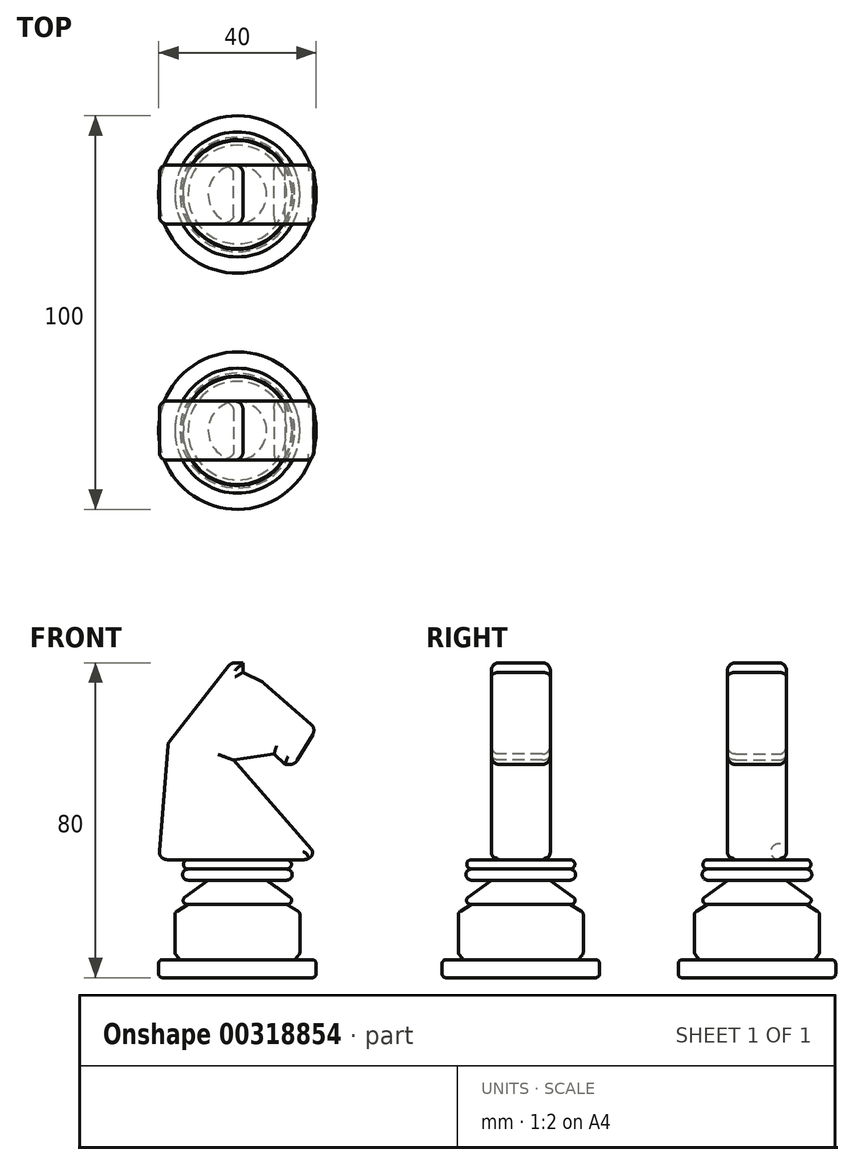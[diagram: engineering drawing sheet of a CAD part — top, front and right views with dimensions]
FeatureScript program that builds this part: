
annotation { "Feature Type Name" : "Feature", "Feature Type Description" : "" }
export const myFeature = defineFeature(function(context is Context, id is Id, definition is map)
    precondition{}
    {
        {
            var Q0;
            Q0=qCreatedBy(makeId("Front.planeOp"),FACE);
            var sketch = newSketch(context, id + "F0", { "sketchPlane" : qUnion([Q0])});
            skLineSegment(sketch, "E0", {"start": v(-20, -50) * mm, "end": v(0, -50) * mm});
            skLineSegment(sketch, "E1", {"start": v(0, -20) * mm, "end": v(-41.16, -20) * mm, "construction": true});
            skLineSegment(sketch, "E2", {"start": v(-20, -50) * mm, "end": v(-20, -45.41) * mm});
            skLineSegment(sketch, "E3", {"start": v(-20, -45.41) * mm, "end": v(-14.57, -45.41) * mm});
            skLineSegment(sketch, "E4", {"start": v(-14.57, -45.41) * mm, "end": v(-15.86, -43.88) * mm});
            skLineSegment(sketch, "E5", {"start": v(-15.86, -43.88) * mm, "end": v(-15.86, -33.4) * mm});
            skLineSegment(sketch, "E6", {"start": v(-15.86, -33.4) * mm, "end": v(-12.53, -31.35) * mm});
            skLineSegment(sketch, "E7", {"start": v(-12.53, -31.35) * mm, "end": v(-15.86, -31.35) * mm});
            skLineSegment(sketch, "E8", {"start": v(-15.86, -31.35) * mm, "end": v(-7.41, -25.21) * mm});
            skLineSegment(sketch, "E9", {"start": v(-7.41, -25.21) * mm, "end": v(-12.53, -25.21) * mm});
            skArc(sketch, "E10", {"start": v(-12.53, -22.4) * mm, "mid": v(-13.93, -23.8) * mm, "end": v(-12.53, -25.21) * mm});
            skLineSegment(sketch, "E11", {"start": v(-12.53, -22.4) * mm, "end": v(-10.23, -22.4) * mm});
            skArc(sketch, "E12", {"start": v(-12.53, -20) * mm, "mid": v(-13.73, -21.2) * mm, "end": v(-12.53, -22.4) * mm});
            skLineSegment(sketch, "E13", {"start": v(-12.53, -20) * mm, "end": v(0, -20) * mm});
            skLineSegment(sketch, "E14", {"start": v(0, -20) * mm, "end": v(0, -50) * mm});
            skLineSegment(sketch, "E15", {"start": v(0, 50.5) * mm, "end": v(0, -69.42) * mm, "construction": true});
            skSolve(sketch);
        }
        {
            var Q0;
            Q0=makeQuery(id+"F0.imprint","IMPRINT",FACE,{"disambiguationData":[TD([[makeQuery(id+"F0.imprint","IMPRINT",EDGE,{"derivedFrom":sQuery(id+"F0.wireOp",EDGE,"E0")}),1.0]])]});
            var Q1;
            Q1=sQuery(id+"F0.wireOp",EDGE,"E15");
            revolve(context, id + "F1", {"entities" : qUnion([Q0]), "axis" : qUnion([Q1]), "revolveType" : RevolveType.FULL});
        }
        {
            var Q0;
            Q0=makeQuery(id+"F1.opRevolve","SWEPT_EDGE",EDGE,{"disambiguationData":[OSD([sQuery(id+"F0.wireOp",EDGE,"E0"),sQuery(id+"F0.wireOp",EDGE,"E2")])]});
            var Q1;
            Q1=makeQuery(id+"F1.opRevolve","SWEPT_EDGE",EDGE,{"disambiguationData":[OSD([sQuery(id+"F0.wireOp",EDGE,"E2"),sQuery(id+"F0.wireOp",EDGE,"E3")])]});
            var Q2;
            Q2=makeQuery(id+"F1.opRevolve","SWEPT_EDGE",EDGE,{"disambiguationData":[OSD([sQuery(id+"F0.wireOp",EDGE,"E5"),sQuery(id+"F0.wireOp",EDGE,"E6")])]});
            var Q3;
            Q3=makeQuery(id+"F1.opRevolve","SWEPT_EDGE",EDGE,{"disambiguationData":[OSD([sQuery(id+"F0.wireOp",EDGE,"E7"),sQuery(id+"F0.wireOp",EDGE,"E8")])]});
            var Q4;
            Q4=makeQuery(id+"F1.opRevolve","SWEPT_EDGE",EDGE,{"disambiguationData":[OSD([sQuery(id+"F0.wireOp",EDGE,"E4"),sQuery(id+"F0.wireOp",EDGE,"E5")])]});
            fillet(context, id + "F2", {"entities" : qUnion([Q0, Q1, Q2, Q3, Q4]), "radius" : 1 * mm, "tangentPropagation" : true, "allowEdgeOverflow" : false});
        }
        {
            var Q0;
            Q0=qCreatedBy(makeId("Front.planeOp"),FACE);
            var sketch = newSketch(context, id + "F3", { "sketchPlane" : qUnion([Q0])});
            skLineSegment(sketch, "E16", {"start": v(-20, -10) * mm, "end": v(-17.6, 19.6) * mm});
            skLineSegment(sketch, "E17", {"start": v(-17.6, 19.6) * mm, "end": v(-1.6, 40) * mm});
            skLineSegment(sketch, "E18", {"start": v(6.6, 35) * mm, "end": v(20, 23.3) * mm});
            skPoint(sketch, "E19.end.orphan", {"position": v(0.26, -10) * mm});
            skLineSegment(sketch, "E20", {"start": v(-20, -10) * mm, "end": v(0.26, -10) * mm});
            skPoint(sketch, "E21.end.orphan", {"position": v(0, 40) * mm});
            skLineSegment(sketch, "E22", {"start": v(-1.6, 40) * mm, "end": v(1.4, 40) * mm});
            skPoint(sketch, "E23.start.orphan", {"position": v(0, 37.6) * mm});
            skLineSegment(sketch, "E24", {"start": v(1.4, 40) * mm, "end": v(1.4, 37.6) * mm});
            skLineSegment(sketch, "E25", {"start": v(1.4, 37.6) * mm, "end": v(6.6, 35) * mm});
            skPoint(sketch, "E26.start.orphan", {"position": v(12.05, 14.2) * mm});
            skLineSegment(sketch, "E27", {"start": v(20, 23.3) * mm, "end": v(14.6, 14.2) * mm});
            skLineSegment(sketch, "E28", {"start": v(14.6, 14.2) * mm, "end": v(11.8, 14.2) * mm});
            skPoint(sketch, "E29.start.orphan", {"position": v(6.6, 16.7) * mm});
            skLineSegment(sketch, "E30", {"start": v(12.05, 14.2) * mm, "end": v(9.3, 16.8) * mm});
            skPoint(sketch, "E31.start.orphan", {"position": v(5.4, 14.2) * mm});
            skLineSegment(sketch, "E32", {"start": v(9.3, 16.8) * mm, "end": v(-1, 15.3) * mm});
            skLineSegment(sketch, "E33", {"start": v(-1, 15.3) * mm, "end": v(20, -8.7) * mm});
            skPoint(sketch, "E34.orphan", {"position": v(19.9, -10) * mm});
            skLineSegment(sketch, "E35", {"start": v(20, -8.7) * mm, "end": v(17.4, -10) * mm});
            skLineSegment(sketch, "E36", {"start": v(17.4, -10) * mm, "end": v(0.26, -10) * mm});
            skSolve(sketch);
        }
        {
            var Q0;
            Q0=makeQuery(id+"F3.imprint","IMPRINT",FACE,{"disambiguationData":[TD([[makeQuery(id+"F3.imprint","IMPRINT",EDGE,{"derivedFrom":sQuery(id+"F3.wireOp",EDGE,"E16")}),-1.0]])]});
            extrude(context, id + "F4", {"entities" : qUnion([Q0]), "operationType" : NewBodyOperationType.ADD, "endBound" : BoundingType.SYMMETRIC, "depth" : 15 * mm});
        }
        {
            var Q0;
            Q0=makeQuery(id+"F4.opExtrude","CAP_FACE",FACE,{"disambiguationData":[OSD([sQuery(id+"F3.wireOp",EDGE,"E16"),sQuery(id+"F3.wireOp",EDGE,"E17"),sQuery(id+"F3.wireOp",EDGE,"E18"),sQuery(id+"F3.wireOp",EDGE,"E20"),sQuery(id+"F3.wireOp",EDGE,"E22"),sQuery(id+"F3.wireOp",EDGE,"E24"),sQuery(id+"F3.wireOp",EDGE,"E25"),sQuery(id+"F3.wireOp",EDGE,"E27"),sQuery(id+"F3.wireOp",EDGE,"E28"),sQuery(id+"F3.wireOp",EDGE,"E30"),sQuery(id+"F3.wireOp",EDGE,"E32"),sQuery(id+"F3.wireOp",EDGE,"E33"),sQuery(id+"F3.wireOp",EDGE,"E35"),sQuery(id+"F3.wireOp",EDGE,"E36")])],"isStart":true});
            var Q1;
            Q1=makeQuery(id+"F4.opExtrude","CAP_FACE",FACE,{"disambiguationData":[OSD([sQuery(id+"F3.wireOp",EDGE,"E16"),sQuery(id+"F3.wireOp",EDGE,"E17"),sQuery(id+"F3.wireOp",EDGE,"E18"),sQuery(id+"F3.wireOp",EDGE,"E20"),sQuery(id+"F3.wireOp",EDGE,"E22"),sQuery(id+"F3.wireOp",EDGE,"E24"),sQuery(id+"F3.wireOp",EDGE,"E25"),sQuery(id+"F3.wireOp",EDGE,"E27"),sQuery(id+"F3.wireOp",EDGE,"E28"),sQuery(id+"F3.wireOp",EDGE,"E30"),sQuery(id+"F3.wireOp",EDGE,"E32"),sQuery(id+"F3.wireOp",EDGE,"E33"),sQuery(id+"F3.wireOp",EDGE,"E35"),sQuery(id+"F3.wireOp",EDGE,"E36")])],"isStart":false});
            var Q2;
            Q2=makeQuery(id+"F4.opExtrude","SWEPT_FACE",FACE,{"disambiguationData":[OSD([sQuery(id+"F3.wireOp",EDGE,"E16")])]});
            var Q3;
            Q3=makeQuery(id+"F4.opExtrude","SWEPT_FACE",FACE,{"disambiguationData":[OSD([sQuery(id+"F3.wireOp",EDGE,"E17")])]});
            var Q4;
            Q4=makeQuery(id+"F4.opExtrude","SWEPT_FACE",FACE,{"disambiguationData":[OSD([sQuery(id+"F3.wireOp",EDGE,"E18")])]});
            var Q5;
            Q5=makeQuery(id+"F4.opExtrude","SWEPT_FACE",FACE,{"disambiguationData":[OSD([sQuery(id+"F3.wireOp",EDGE,"E27")])]});
            fillet(context, id + "F5", {"entities" : qUnion([Q0, Q1, Q2, Q3, Q4, Q5]), "radius" : 2 * mm, "allowEdgeOverflow" : false});
        }
        {
            var Q0;
            Q0=makeQuery(id+"F4.opExtrude","SWEPT_FACE",FACE,{"disambiguationData":[OSD([sQuery(id+"F3.wireOp",EDGE,"E35")])]});
            fillet(context, id + "F6", {"entities" : qUnion([Q0]), "radius" : 1.5 * mm, "tangentPropagation" : true, "allowEdgeOverflow" : false});
        }
        {
            var Q0;
            Q0=makeQuery(id+"F4.opExtrude","SWEPT_BODY",BODY,{"disambiguationData":[OSD([sQuery(id+"F3.wireOp",EDGE,"E16"),sQuery(id+"F3.wireOp",EDGE,"E17"),sQuery(id+"F3.wireOp",EDGE,"E18"),sQuery(id+"F3.wireOp",EDGE,"E20"),sQuery(id+"F3.wireOp",EDGE,"E22"),sQuery(id+"F3.wireOp",EDGE,"E24"),sQuery(id+"F3.wireOp",EDGE,"E25"),sQuery(id+"F3.wireOp",EDGE,"E27"),sQuery(id+"F3.wireOp",EDGE,"E28"),sQuery(id+"F3.wireOp",EDGE,"E30"),sQuery(id+"F3.wireOp",EDGE,"E32"),sQuery(id+"F3.wireOp",EDGE,"E33"),sQuery(id+"F3.wireOp",EDGE,"E35"),sQuery(id+"F3.wireOp",EDGE,"E36")])]});
            transform(context, id + "F7", {"entities" : qUnion([Q0]), "transformType" : TransformType.TRANSLATION_3D, "dx" : 0 * mm, "dy" : 0 * mm, "dz" : -10 * mm, "makeCopy" : false});
        }
        {
            var Q0;
            Q0=qCreatedBy(makeId("Front.planeOp"),FACE);
            cPlane(context, id + "F8", {"entities" : qUnion([Q0]), "cplaneType" : CPlaneType.OFFSET, "offset" : 30 * mm, "width" : 150 * mm, "height" : 150 * mm});
        }
        {
            var Q0;
            Q0=makeQuery(id+"F4.opExtrude","SWEPT_BODY",BODY,{"disambiguationData":[OSD([sQuery(id+"F3.wireOp",EDGE,"E16"),sQuery(id+"F3.wireOp",EDGE,"E17"),sQuery(id+"F3.wireOp",EDGE,"E18"),sQuery(id+"F3.wireOp",EDGE,"E20"),sQuery(id+"F3.wireOp",EDGE,"E22"),sQuery(id+"F3.wireOp",EDGE,"E24"),sQuery(id+"F3.wireOp",EDGE,"E25"),sQuery(id+"F3.wireOp",EDGE,"E27"),sQuery(id+"F3.wireOp",EDGE,"E28"),sQuery(id+"F3.wireOp",EDGE,"E30"),sQuery(id+"F3.wireOp",EDGE,"E32"),sQuery(id+"F3.wireOp",EDGE,"E33"),sQuery(id+"F3.wireOp",EDGE,"E35"),sQuery(id+"F3.wireOp",EDGE,"E36")])]});
            var Q1;
            Q1=makeQuery(id+"F1.opRevolve","SWEPT_BODY",BODY,{"disambiguationData":[OSD([sQuery(id+"F0.wireOp",EDGE,"E0"),sQuery(id+"F0.wireOp",EDGE,"E2"),sQuery(id+"F0.wireOp",EDGE,"E3"),sQuery(id+"F0.wireOp",EDGE,"E4"),sQuery(id+"F0.wireOp",EDGE,"E5"),sQuery(id+"F0.wireOp",EDGE,"E6"),sQuery(id+"F0.wireOp",EDGE,"E7"),sQuery(id+"F0.wireOp",EDGE,"E8"),sQuery(id+"F0.wireOp",EDGE,"E9"),sQuery(id+"F0.wireOp",EDGE,"E10"),sQuery(id+"F0.wireOp",EDGE,"E12"),sQuery(id+"F0.wireOp",EDGE,"E13"),sQuery(id+"F0.wireOp",EDGE,"E14")])]});
            var Q2;
            Q2=qCreatedBy(id+"F8.planeOp",FACE);
            mirror(context, id + "F9", {"entities" : qUnion([Q0, Q1]), "mirrorPlane" : qUnion([Q2])});
        }
    });
